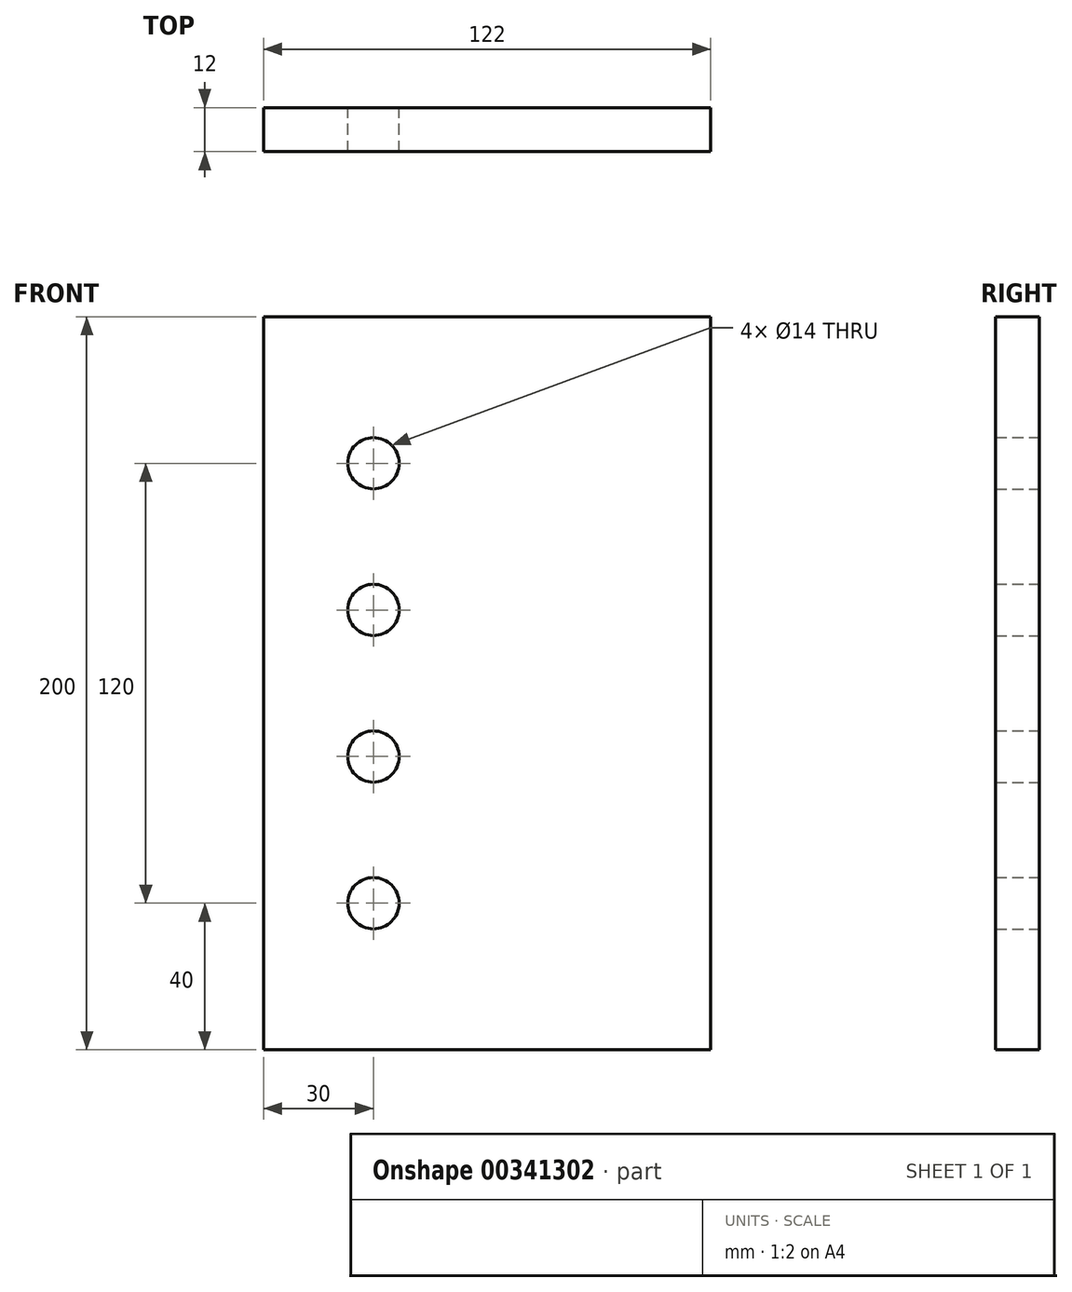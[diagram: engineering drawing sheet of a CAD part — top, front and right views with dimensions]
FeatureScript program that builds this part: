
annotation { "Feature Type Name" : "Feature", "Feature Type Description" : "" }
export const myFeature = defineFeature(function(context is Context, id is Id, definition is map)
    precondition{}
    {
        {
            var Q0;
            Q0=qCreatedBy(makeId("Front.planeOp"),FACE);
            var sketch = newSketch(context, id + "F0", { "sketchPlane" : qUnion([Q0])});
            skLineSegment(sketch, "E0.bottom", {"start": v(0, 0) * mm, "end": v(122, 0) * mm});
            skLineSegment(sketch, "E0.top", {"start": v(0, 200) * mm, "end": v(122, 200) * mm});
            skLineSegment(sketch, "E0.left", {"start": v(0, 0) * mm, "end": v(0, 200) * mm});
            skLineSegment(sketch, "E0.right", {"start": v(122, 0) * mm, "end": v(122, 200) * mm});
            skSolve(sketch);
        }
        {
            var Q0;
            Q0=makeQuery(id+"F0.imprint","IMPRINT",FACE,{"disambiguationData":[TD([[makeQuery(id+"F0.imprint","IMPRINT",EDGE,{"derivedFrom":sQuery(id+"F0.wireOp",EDGE,"E0.bottom")}),1.0]])]});
            extrude(context, id + "F1", {"entities" : qUnion([Q0]), "depth" : 12 * mm});
        }
        {
            var Q0;
            Q0=makeQuery(id+"F1.opExtrude","CAP_FACE",FACE,{"disambiguationData":[OSD([sQuery(id+"F0.wireOp",EDGE,"E0.bottom"),sQuery(id+"F0.wireOp",EDGE,"E0.top"),sQuery(id+"F0.wireOp",EDGE,"E0.left"),sQuery(id+"F0.wireOp",EDGE,"E0.right")])],"isStart":false});
            var sketch = newSketch(context, id + "F2", { "sketchPlane" : qUnion([Q0])});
            skPoint(sketch, "E1", {"position": v(30, 160) * mm});
            skPoint(sketch, "E2", {"position": v(30, 120) * mm});
            skPoint(sketch, "E3", {"position": v(30, 80) * mm});
            skPoint(sketch, "E4", {"position": v(30, 40) * mm});
            skSolve(sketch);
        }
        {
            var Q0;
            Q0=sQuery(id+"F2.wireOp",VERTEX,"E1");
            var Q1;
            Q1=sQuery(id+"F2.wireOp",VERTEX,"E2");
            var Q2;
            Q2=sQuery(id+"F2.wireOp",VERTEX,"E3");
            var Q3;
            Q3=sQuery(id+"F2.wireOp",VERTEX,"E4");
            var Q4;
            Q4=makeQuery(id+"F1.opExtrude","SWEPT_BODY",BODY,{"disambiguationData":[OSD([sQuery(id+"F0.wireOp",EDGE,"E0.bottom"),sQuery(id+"F0.wireOp",EDGE,"E0.top"),sQuery(id+"F0.wireOp",EDGE,"E0.left"),sQuery(id+"F0.wireOp",EDGE,"E0.right")])]});
            hole(context, id + "F3", {"style" : HoleStyle.SIMPLE, "endStyle" : HoleEndStyle.THROUGH, "holeDiameter" : 14 * mm, "tappedDepth" : 12 * mm, "tapClearance" : 3, "locations" : qUnion([Q0, Q1, Q2, Q3]), "scope" : qUnion([Q4]), "startStyle" : HoleStartStyle.PART});
        }
    });
